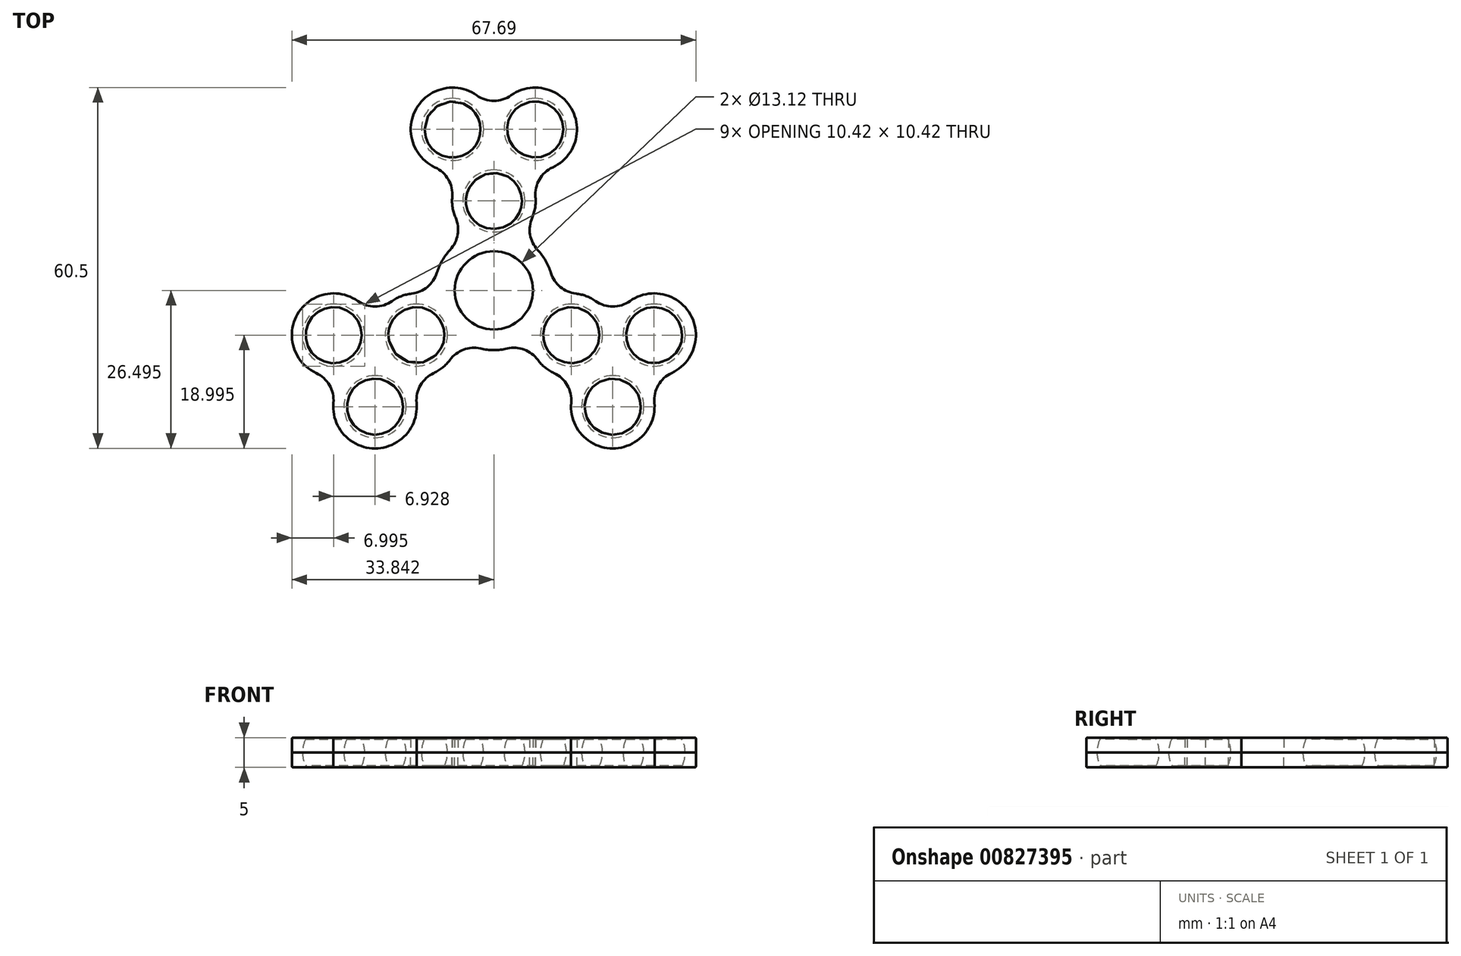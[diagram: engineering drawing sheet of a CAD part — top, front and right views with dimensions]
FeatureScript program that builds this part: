
annotation { "Feature Type Name" : "Feature", "Feature Type Description" : "" }
export const myFeature = defineFeature(function(context is Context, id is Id, definition is map)
    precondition{}
    {
        {
            var Q0;
            Q0=qCreatedBy(makeId("Top.planeOp"),FACE);
            var sketch = newSketch(context, id + "F0", { "sketchPlane" : qUnion([Q0])});
            skCircle(sketch, "E0", {"center": v(73.24, 0.6) * mm, "radius": 6.56 * mm});
            skArc(sketch, "E1", {"start": v(65.9, 7.4) * mm, "mid": v(64.58, 5.6) * mm, "end": v(63.69, 3.55) * mm});
            skCircle(sketch, "E2", {"center": v(73.24, 15.6) * mm, "radius": 2.5 * mm});
            skCircle(sketch, "E3", {"center": v(60.25, -6.9) * mm, "radius": 2.5 * mm});
            skCircle(sketch, "E4", {"center": v(86.23, -6.9) * mm, "radius": 2.5 * mm});
            skCircle(sketch, "E5", {"center": v(80.17, 27.6) * mm, "radius": 2.5 * mm});
            skCircle(sketch, "E6", {"center": v(66.31, 27.6) * mm, "radius": 2.5 * mm});
            skCircle(sketch, "E7", {"center": v(46.4, -6.9) * mm, "radius": 2.5 * mm});
            skCircle(sketch, "E8", {"center": v(53.32, -18.9) * mm, "radius": 2.5 * mm});
            skCircle(sketch, "E9", {"center": v(93.16, -18.9) * mm, "radius": 2.5 * mm});
            skCircle(sketch, "E10", {"center": v(100.09, -6.9) * mm, "radius": 2.5 * mm});
            skArc(sketch, "E11", {"start": v(66.27, 16.25) * mm, "mid": v(66.33, 14.5) * mm, "end": v(66.83, 12.8) * mm});
            skArc(sketch, "E12", {"start": v(70.36, 33.32) * mm, "mid": v(60.25, 31.1) * mm, "end": v(63.38, 21.25) * mm});
            skArc(sketch, "E13", {"start": v(83.1, 21.25) * mm, "mid": v(86.23, 31.1) * mm, "end": v(76.13, 33.32) * mm});
            skPoint(sketch, "E14.visualSharp", {"position": v(73.24, 28.6) * mm});
            skArc(sketch, "E14.filletArc", {"start": v(70.36, 33.32) * mm, "mid": v(73.24, 32.4) * mm, "end": v(76.13, 33.32) * mm});
            skPoint(sketch, "E15.visualSharp", {"position": v(68.91, 21.1) * mm});
            skArc(sketch, "E15.filletArc", {"start": v(66.27, 16.25) * mm, "mid": v(65.62, 19.2) * mm, "end": v(63.38, 21.25) * mm});
            skPoint(sketch, "E16.visualSharp", {"position": v(77.57, 21.1) * mm});
            skArc(sketch, "E16.filletArc", {"start": v(83.1, 21.25) * mm, "mid": v(80.86, 19.2) * mm, "end": v(80.21, 16.25) * mm});
            skArc(sketch, "E17.trimOffspring", {"start": v(79.66, 12.8) * mm, "mid": v(80.15, 14.5) * mm, "end": v(80.21, 16.25) * mm});
            skArc(sketch, "E18", {"start": v(63.18, -13.25) * mm, "mid": v(64.67, -12.32) * mm, "end": v(65.88, -11.05) * mm});
            skArc(sketch, "E19", {"start": v(46.35, -18.25) * mm, "mid": v(53.32, -25.9) * mm, "end": v(60.3, -18.25) * mm});
            skArc(sketch, "E20", {"start": v(50.44, -1.18) * mm, "mid": v(40.33, -3.4) * mm, "end": v(43.47, -13.25) * mm});
            skArc(sketch, "E21.filletArc", {"start": v(46.35, -18.25) * mm, "mid": v(45.7, -15.3) * mm, "end": v(43.47, -13.25) * mm});
            skArc(sketch, "E22.filletArc", {"start": v(63.18, -13.25) * mm, "mid": v(60.94, -15.3) * mm, "end": v(60.3, -18.25) * mm});
            skArc(sketch, "E23.filletArc", {"start": v(50.44, -1.18) * mm, "mid": v(53.32, -2.1) * mm, "end": v(56.21, -1.18) * mm});
            skArc(sketch, "E24.trimOffspring", {"start": v(59.47, 0.06) * mm, "mid": v(57.76, -0.35) * mm, "end": v(56.21, -1.18) * mm});
            skArc(sketch, "E25", {"start": v(90.27, -1.18) * mm, "mid": v(88.72, -0.35) * mm, "end": v(87.02, 0.06) * mm});
            skArc(sketch, "E26", {"start": v(103.02, -13.25) * mm, "mid": v(106.15, -3.4) * mm, "end": v(96.05, -1.18) * mm});
            skArc(sketch, "E27", {"start": v(86.2, -18.25) * mm, "mid": v(93.16, -25.9) * mm, "end": v(100.13, -18.25) * mm});
            skArc(sketch, "E28.filletArc", {"start": v(103.02, -13.25) * mm, "mid": v(100.78, -15.3) * mm, "end": v(100.13, -18.25) * mm});
            skArc(sketch, "E29.filletArc", {"start": v(90.27, -1.18) * mm, "mid": v(93.16, -2.1) * mm, "end": v(96.05, -1.18) * mm});
            skArc(sketch, "E30.filletArc", {"start": v(86.2, -18.25) * mm, "mid": v(85.54, -15.3) * mm, "end": v(83.3, -13.25) * mm});
            skArc(sketch, "E31.trimOffspring", {"start": v(80.6, -11.05) * mm, "mid": v(81.81, -12.32) * mm, "end": v(83.3, -13.25) * mm});
            skArc(sketch, "E32.trimOffspring", {"start": v(71.02, -9.14) * mm, "mid": v(73.24, -9.4) * mm, "end": v(75.46, -9.14) * mm});
            skArc(sketch, "E33.trimOffspring", {"start": v(82.8, 3.55) * mm, "mid": v(81.9, 5.6) * mm, "end": v(80.57, 7.4) * mm});
            skPoint(sketch, "E34.visualSharp", {"position": v(63.31, -0.6) * mm});
            skArc(sketch, "E34.filletArc", {"start": v(59.47, 0.06) * mm, "mid": v(62.1, 1.18) * mm, "end": v(63.69, 3.55) * mm});
            skPoint(sketch, "E35.visualSharp", {"position": v(67.23, -7.39) * mm});
            skArc(sketch, "E35.filletArc", {"start": v(71.02, -9.14) * mm, "mid": v(68.17, -9.33) * mm, "end": v(65.88, -11.05) * mm});
            skPoint(sketch, "E36.visualSharp", {"position": v(79.25, -7.39) * mm});
            skArc(sketch, "E36.filletArc", {"start": v(80.6, -11.05) * mm, "mid": v(78.32, -9.33) * mm, "end": v(75.46, -9.14) * mm});
            skPoint(sketch, "E37.visualSharp", {"position": v(83.17, -0.6) * mm});
            skArc(sketch, "E37.filletArc", {"start": v(82.8, 3.55) * mm, "mid": v(84.39, 1.18) * mm, "end": v(87.02, 0.06) * mm});
            skPoint(sketch, "E38.visualSharp", {"position": v(77.16, 9.8) * mm});
            skArc(sketch, "E38.filletArc", {"start": v(79.66, 12.8) * mm, "mid": v(79.31, 9.97) * mm, "end": v(80.57, 7.4) * mm});
            skPoint(sketch, "E39.visualSharp", {"position": v(69.32, 9.8) * mm});
            skArc(sketch, "E39.filletArc", {"start": v(65.9, 7.4) * mm, "mid": v(67.17, 9.97) * mm, "end": v(66.83, 12.8) * mm});
            skSolve(sketch);
        }
        {
            var Q0;
            Q0=qSketchRegion(id+"F0",true);
            extrude(context, id + "F1", {"entities" : qUnion([Q0]), "depth" : 2.5 * mm, "offsetDistance" : 25 * mm});
        }
        {
            var Q0;
            Q0=makeQuery(id+"F0.imprint","IMPRINT",FACE,{"disambiguationData":[TD([[makeQuery(id+"F0.imprint","IMPRINT",EDGE,{"derivedFrom":sQuery(id+"F0.wireOp",EDGE,"E0")}),-1.0]])]});
            extrude(context, id + "F2", {"entities" : qUnion([Q0]), "oppositeDirection" : true, "depth" : 2.5 * mm, "offsetDistance" : 25 * mm});
        }
        {
            var Q0;
            Q0=makeQuery(id+"F2.opExtrude","CAP_FACE",FACE,{"disambiguationData":[OSD([sQuery(id+"F0.wireOp",EDGE,"E0"),sQuery(id+"F0.wireOp",EDGE,"E1"),sQuery(id+"F0.wireOp",EDGE,"E2"),sQuery(id+"F0.wireOp",EDGE,"E3"),sQuery(id+"F0.wireOp",EDGE,"E4"),sQuery(id+"F0.wireOp",EDGE,"E5"),sQuery(id+"F0.wireOp",EDGE,"E6"),sQuery(id+"F0.wireOp",EDGE,"E7"),sQuery(id+"F0.wireOp",EDGE,"E8"),sQuery(id+"F0.wireOp",EDGE,"E9"),sQuery(id+"F0.wireOp",EDGE,"E10"),sQuery(id+"F0.wireOp",EDGE,"E11"),sQuery(id+"F0.wireOp",EDGE,"E12"),sQuery(id+"F0.wireOp",EDGE,"E13"),sQuery(id+"F0.wireOp",EDGE,"E14.filletArc"),sQuery(id+"F0.wireOp",EDGE,"E15.filletArc"),sQuery(id+"F0.wireOp",EDGE,"E16.filletArc"),sQuery(id+"F0.wireOp",EDGE,"E17.trimOffspring"),sQuery(id+"F0.wireOp",EDGE,"E18"),sQuery(id+"F0.wireOp",EDGE,"E19"),sQuery(id+"F0.wireOp",EDGE,"E20"),sQuery(id+"F0.wireOp",EDGE,"E21.filletArc"),sQuery(id+"F0.wireOp",EDGE,"E22.filletArc"),sQuery(id+"F0.wireOp",EDGE,"E23.filletArc"),sQuery(id+"F0.wireOp",EDGE,"E24.trimOffspring"),sQuery(id+"F0.wireOp",EDGE,"E25"),sQuery(id+"F0.wireOp",EDGE,"E26"),sQuery(id+"F0.wireOp",EDGE,"E27"),sQuery(id+"F0.wireOp",EDGE,"E28.filletArc"),sQuery(id+"F0.wireOp",EDGE,"E29.filletArc"),sQuery(id+"F0.wireOp",EDGE,"E30.filletArc"),sQuery(id+"F0.wireOp",EDGE,"E31.trimOffspring"),sQuery(id+"F0.wireOp",EDGE,"E32.trimOffspring"),sQuery(id+"F0.wireOp",EDGE,"E33.trimOffspring"),sQuery(id+"F0.wireOp",EDGE,"E34.filletArc"),sQuery(id+"F0.wireOp",EDGE,"E35.filletArc"),sQuery(id+"F0.wireOp",EDGE,"E36.filletArc"),sQuery(id+"F0.wireOp",EDGE,"E37.filletArc"),sQuery(id+"F0.wireOp",EDGE,"E38.filletArc"),sQuery(id+"F0.wireOp",EDGE,"E39.filletArc")])],"isStart":true});
            var sketch = newSketch(context, id + "F3", { "sketchPlane" : qUnion([Q0])});
            skLineSegment(sketch, "E40", {"start": v(53.32, -18.9) * mm, "end": v(53.32, -24.1) * mm});
            skLineSegment(sketch, "E41", {"start": v(53.32, -18.9) * mm, "end": v(53.32, -13.68) * mm});
            skArc(sketch, "E42", {"start": v(53.32, -13.68) * mm, "mid": v(48.11, -18.9) * mm, "end": v(53.32, -24.1) * mm});
            skSolve(sketch);
        }
        {
            var Q0;
            Q0=qSketchRegion(id+"F3",true);
            var Q1;
            Q1=sQuery(id+"F3.wireOp",EDGE,"E41");
            revolve(context, id + "F4", {"surfaceOperationType" : NewSurfaceOperationType.NEW, "entities" : qUnion([Q0]), "axis" : qUnion([Q1]), "revolveType" : RevolveType.FULL});
        }
        {
            var Q0;
            Q0=makeQuery(id+"F2.opExtrude","CAP_FACE",FACE,{"disambiguationData":[OSD([sQuery(id+"F0.wireOp",EDGE,"E0"),sQuery(id+"F0.wireOp",EDGE,"E1"),sQuery(id+"F0.wireOp",EDGE,"E2"),sQuery(id+"F0.wireOp",EDGE,"E3"),sQuery(id+"F0.wireOp",EDGE,"E4"),sQuery(id+"F0.wireOp",EDGE,"E5"),sQuery(id+"F0.wireOp",EDGE,"E6"),sQuery(id+"F0.wireOp",EDGE,"E7"),sQuery(id+"F0.wireOp",EDGE,"E8"),sQuery(id+"F0.wireOp",EDGE,"E9"),sQuery(id+"F0.wireOp",EDGE,"E10"),sQuery(id+"F0.wireOp",EDGE,"E11"),sQuery(id+"F0.wireOp",EDGE,"E12"),sQuery(id+"F0.wireOp",EDGE,"E13"),sQuery(id+"F0.wireOp",EDGE,"E14.filletArc"),sQuery(id+"F0.wireOp",EDGE,"E15.filletArc"),sQuery(id+"F0.wireOp",EDGE,"E16.filletArc"),sQuery(id+"F0.wireOp",EDGE,"E17.trimOffspring"),sQuery(id+"F0.wireOp",EDGE,"E18"),sQuery(id+"F0.wireOp",EDGE,"E19"),sQuery(id+"F0.wireOp",EDGE,"E20"),sQuery(id+"F0.wireOp",EDGE,"E21.filletArc"),sQuery(id+"F0.wireOp",EDGE,"E22.filletArc"),sQuery(id+"F0.wireOp",EDGE,"E23.filletArc"),sQuery(id+"F0.wireOp",EDGE,"E24.trimOffspring"),sQuery(id+"F0.wireOp",EDGE,"E25"),sQuery(id+"F0.wireOp",EDGE,"E26"),sQuery(id+"F0.wireOp",EDGE,"E27"),sQuery(id+"F0.wireOp",EDGE,"E28.filletArc"),sQuery(id+"F0.wireOp",EDGE,"E29.filletArc"),sQuery(id+"F0.wireOp",EDGE,"E30.filletArc"),sQuery(id+"F0.wireOp",EDGE,"E31.trimOffspring"),sQuery(id+"F0.wireOp",EDGE,"E32.trimOffspring"),sQuery(id+"F0.wireOp",EDGE,"E33.trimOffspring"),sQuery(id+"F0.wireOp",EDGE,"E34.filletArc"),sQuery(id+"F0.wireOp",EDGE,"E35.filletArc"),sQuery(id+"F0.wireOp",EDGE,"E36.filletArc"),sQuery(id+"F0.wireOp",EDGE,"E37.filletArc"),sQuery(id+"F0.wireOp",EDGE,"E38.filletArc"),sQuery(id+"F0.wireOp",EDGE,"E39.filletArc")])],"isStart":true});
            var sketch = newSketch(context, id + "F5", { "sketchPlane" : qUnion([Q0])});
            skLineSegment(sketch, "E43", {"start": v(60.25, -6.9) * mm, "end": v(60.25, -12.1) * mm});
            skLineSegment(sketch, "E44", {"start": v(60.25, -6.9) * mm, "end": v(60.25, -1.68) * mm});
            skArc(sketch, "E45", {"start": v(60.25, -1.68) * mm, "mid": v(55.04, -6.9) * mm, "end": v(60.25, -12.1) * mm});
            skSolve(sketch);
        }
        {
            var Q0;
            Q0=makeQuery(id+"F2.opExtrude","CAP_FACE",FACE,{"disambiguationData":[OSD([sQuery(id+"F0.wireOp",EDGE,"E0"),sQuery(id+"F0.wireOp",EDGE,"E1"),sQuery(id+"F0.wireOp",EDGE,"E2"),sQuery(id+"F0.wireOp",EDGE,"E3"),sQuery(id+"F0.wireOp",EDGE,"E4"),sQuery(id+"F0.wireOp",EDGE,"E5"),sQuery(id+"F0.wireOp",EDGE,"E6"),sQuery(id+"F0.wireOp",EDGE,"E7"),sQuery(id+"F0.wireOp",EDGE,"E8"),sQuery(id+"F0.wireOp",EDGE,"E9"),sQuery(id+"F0.wireOp",EDGE,"E10"),sQuery(id+"F0.wireOp",EDGE,"E11"),sQuery(id+"F0.wireOp",EDGE,"E12"),sQuery(id+"F0.wireOp",EDGE,"E13"),sQuery(id+"F0.wireOp",EDGE,"E14.filletArc"),sQuery(id+"F0.wireOp",EDGE,"E15.filletArc"),sQuery(id+"F0.wireOp",EDGE,"E16.filletArc"),sQuery(id+"F0.wireOp",EDGE,"E17.trimOffspring"),sQuery(id+"F0.wireOp",EDGE,"E18"),sQuery(id+"F0.wireOp",EDGE,"E19"),sQuery(id+"F0.wireOp",EDGE,"E20"),sQuery(id+"F0.wireOp",EDGE,"E21.filletArc"),sQuery(id+"F0.wireOp",EDGE,"E22.filletArc"),sQuery(id+"F0.wireOp",EDGE,"E23.filletArc"),sQuery(id+"F0.wireOp",EDGE,"E24.trimOffspring"),sQuery(id+"F0.wireOp",EDGE,"E25"),sQuery(id+"F0.wireOp",EDGE,"E26"),sQuery(id+"F0.wireOp",EDGE,"E27"),sQuery(id+"F0.wireOp",EDGE,"E28.filletArc"),sQuery(id+"F0.wireOp",EDGE,"E29.filletArc"),sQuery(id+"F0.wireOp",EDGE,"E30.filletArc"),sQuery(id+"F0.wireOp",EDGE,"E31.trimOffspring"),sQuery(id+"F0.wireOp",EDGE,"E32.trimOffspring"),sQuery(id+"F0.wireOp",EDGE,"E33.trimOffspring"),sQuery(id+"F0.wireOp",EDGE,"E34.filletArc"),sQuery(id+"F0.wireOp",EDGE,"E35.filletArc"),sQuery(id+"F0.wireOp",EDGE,"E36.filletArc"),sQuery(id+"F0.wireOp",EDGE,"E37.filletArc"),sQuery(id+"F0.wireOp",EDGE,"E38.filletArc"),sQuery(id+"F0.wireOp",EDGE,"E39.filletArc")])],"isStart":true});
            var sketch = newSketch(context, id + "F6", { "sketchPlane" : qUnion([Q0])});
            skLineSegment(sketch, "E46", {"start": v(93.16, -18.9) * mm, "end": v(93.16, -24.1) * mm});
            skArc(sketch, "E47", {"start": v(93.16, -13.68) * mm, "mid": v(87.95, -18.9) * mm, "end": v(93.16, -24.1) * mm});
            skLineSegment(sketch, "E48", {"start": v(93.16, -18.9) * mm, "end": v(93.16, -13.68) * mm});
            skSolve(sketch);
        }
        {
            var Q0;
            Q0=qSketchRegion(id+"F6",true);
            var Q1;
            Q1=sQuery(id+"F6.wireOp",EDGE,"E48");
            revolve(context, id + "F7", {"surfaceOperationType" : NewSurfaceOperationType.NEW, "entities" : qUnion([Q0]), "axis" : qUnion([Q1]), "revolveType" : RevolveType.FULL});
        }
        {
            var Q0;
            Q0=makeQuery(id+"F2.opExtrude","CAP_FACE",FACE,{"disambiguationData":[OSD([sQuery(id+"F0.wireOp",EDGE,"E0"),sQuery(id+"F0.wireOp",EDGE,"E1"),sQuery(id+"F0.wireOp",EDGE,"E2"),sQuery(id+"F0.wireOp",EDGE,"E3"),sQuery(id+"F0.wireOp",EDGE,"E4"),sQuery(id+"F0.wireOp",EDGE,"E5"),sQuery(id+"F0.wireOp",EDGE,"E6"),sQuery(id+"F0.wireOp",EDGE,"E7"),sQuery(id+"F0.wireOp",EDGE,"E8"),sQuery(id+"F0.wireOp",EDGE,"E9"),sQuery(id+"F0.wireOp",EDGE,"E10"),sQuery(id+"F0.wireOp",EDGE,"E11"),sQuery(id+"F0.wireOp",EDGE,"E12"),sQuery(id+"F0.wireOp",EDGE,"E13"),sQuery(id+"F0.wireOp",EDGE,"E14.filletArc"),sQuery(id+"F0.wireOp",EDGE,"E15.filletArc"),sQuery(id+"F0.wireOp",EDGE,"E16.filletArc"),sQuery(id+"F0.wireOp",EDGE,"E17.trimOffspring"),sQuery(id+"F0.wireOp",EDGE,"E18"),sQuery(id+"F0.wireOp",EDGE,"E19"),sQuery(id+"F0.wireOp",EDGE,"E20"),sQuery(id+"F0.wireOp",EDGE,"E21.filletArc"),sQuery(id+"F0.wireOp",EDGE,"E22.filletArc"),sQuery(id+"F0.wireOp",EDGE,"E23.filletArc"),sQuery(id+"F0.wireOp",EDGE,"E24.trimOffspring"),sQuery(id+"F0.wireOp",EDGE,"E25"),sQuery(id+"F0.wireOp",EDGE,"E26"),sQuery(id+"F0.wireOp",EDGE,"E27"),sQuery(id+"F0.wireOp",EDGE,"E28.filletArc"),sQuery(id+"F0.wireOp",EDGE,"E29.filletArc"),sQuery(id+"F0.wireOp",EDGE,"E30.filletArc"),sQuery(id+"F0.wireOp",EDGE,"E31.trimOffspring"),sQuery(id+"F0.wireOp",EDGE,"E32.trimOffspring"),sQuery(id+"F0.wireOp",EDGE,"E33.trimOffspring"),sQuery(id+"F0.wireOp",EDGE,"E34.filletArc"),sQuery(id+"F0.wireOp",EDGE,"E35.filletArc"),sQuery(id+"F0.wireOp",EDGE,"E36.filletArc"),sQuery(id+"F0.wireOp",EDGE,"E37.filletArc"),sQuery(id+"F0.wireOp",EDGE,"E38.filletArc"),sQuery(id+"F0.wireOp",EDGE,"E39.filletArc")])],"isStart":true});
            var sketch = newSketch(context, id + "F8", { "sketchPlane" : qUnion([Q0])});
            skLineSegment(sketch, "E49", {"start": v(86.23, -6.9) * mm, "end": v(86.23, -12.1) * mm});
            skArc(sketch, "E50", {"start": v(86.23, -1.68) * mm, "mid": v(81.02, -6.9) * mm, "end": v(86.23, -12.1) * mm});
            skLineSegment(sketch, "E51", {"start": v(86.23, -6.9) * mm, "end": v(86.23, -1.68) * mm});
            skSolve(sketch);
        }
        {
            var Q0;
            Q0=qSketchRegion(id+"F8",true);
            var Q1;
            Q1=sQuery(id+"F8.wireOp",EDGE,"E51");
            revolve(context, id + "F9", {"surfaceOperationType" : NewSurfaceOperationType.NEW, "entities" : qUnion([Q0]), "axis" : qUnion([Q1]), "revolveType" : RevolveType.FULL});
        }
        {
            var Q0;
            Q0=makeQuery(id+"F2.opExtrude","CAP_FACE",FACE,{"disambiguationData":[OSD([sQuery(id+"F0.wireOp",EDGE,"E0"),sQuery(id+"F0.wireOp",EDGE,"E1"),sQuery(id+"F0.wireOp",EDGE,"E2"),sQuery(id+"F0.wireOp",EDGE,"E3"),sQuery(id+"F0.wireOp",EDGE,"E4"),sQuery(id+"F0.wireOp",EDGE,"E5"),sQuery(id+"F0.wireOp",EDGE,"E6"),sQuery(id+"F0.wireOp",EDGE,"E7"),sQuery(id+"F0.wireOp",EDGE,"E8"),sQuery(id+"F0.wireOp",EDGE,"E9"),sQuery(id+"F0.wireOp",EDGE,"E10"),sQuery(id+"F0.wireOp",EDGE,"E11"),sQuery(id+"F0.wireOp",EDGE,"E12"),sQuery(id+"F0.wireOp",EDGE,"E13"),sQuery(id+"F0.wireOp",EDGE,"E14.filletArc"),sQuery(id+"F0.wireOp",EDGE,"E15.filletArc"),sQuery(id+"F0.wireOp",EDGE,"E16.filletArc"),sQuery(id+"F0.wireOp",EDGE,"E17.trimOffspring"),sQuery(id+"F0.wireOp",EDGE,"E18"),sQuery(id+"F0.wireOp",EDGE,"E19"),sQuery(id+"F0.wireOp",EDGE,"E20"),sQuery(id+"F0.wireOp",EDGE,"E21.filletArc"),sQuery(id+"F0.wireOp",EDGE,"E22.filletArc"),sQuery(id+"F0.wireOp",EDGE,"E23.filletArc"),sQuery(id+"F0.wireOp",EDGE,"E24.trimOffspring"),sQuery(id+"F0.wireOp",EDGE,"E25"),sQuery(id+"F0.wireOp",EDGE,"E26"),sQuery(id+"F0.wireOp",EDGE,"E27"),sQuery(id+"F0.wireOp",EDGE,"E28.filletArc"),sQuery(id+"F0.wireOp",EDGE,"E29.filletArc"),sQuery(id+"F0.wireOp",EDGE,"E30.filletArc"),sQuery(id+"F0.wireOp",EDGE,"E31.trimOffspring"),sQuery(id+"F0.wireOp",EDGE,"E32.trimOffspring"),sQuery(id+"F0.wireOp",EDGE,"E33.trimOffspring"),sQuery(id+"F0.wireOp",EDGE,"E34.filletArc"),sQuery(id+"F0.wireOp",EDGE,"E35.filletArc"),sQuery(id+"F0.wireOp",EDGE,"E36.filletArc"),sQuery(id+"F0.wireOp",EDGE,"E37.filletArc"),sQuery(id+"F0.wireOp",EDGE,"E38.filletArc"),sQuery(id+"F0.wireOp",EDGE,"E39.filletArc")])],"isStart":true});
            var sketch = newSketch(context, id + "F10", { "sketchPlane" : qUnion([Q0])});
            skLineSegment(sketch, "E52", {"start": v(100.09, -6.9) * mm, "end": v(100.09, -12.1) * mm});
            skArc(sketch, "E53", {"start": v(100.09, -1.68) * mm, "mid": v(94.88, -6.9) * mm, "end": v(100.09, -12.1) * mm});
            skLineSegment(sketch, "E54", {"start": v(100.09, -6.9) * mm, "end": v(100.09, -1.68) * mm});
            skSolve(sketch);
        }
        {
            var Q0;
            Q0=qSketchRegion(id+"F10",true);
            var Q1;
            Q1=sQuery(id+"F10.wireOp",EDGE,"E52");
            revolve(context, id + "F11", {"surfaceOperationType" : NewSurfaceOperationType.NEW, "entities" : qUnion([Q0]), "axis" : qUnion([Q1]), "revolveType" : RevolveType.FULL});
        }
        {
            var Q0;
            Q0=makeQuery(id+"F2.opExtrude","CAP_FACE",FACE,{"disambiguationData":[OSD([sQuery(id+"F0.wireOp",EDGE,"E0"),sQuery(id+"F0.wireOp",EDGE,"E1"),sQuery(id+"F0.wireOp",EDGE,"E2"),sQuery(id+"F0.wireOp",EDGE,"E3"),sQuery(id+"F0.wireOp",EDGE,"E4"),sQuery(id+"F0.wireOp",EDGE,"E5"),sQuery(id+"F0.wireOp",EDGE,"E6"),sQuery(id+"F0.wireOp",EDGE,"E7"),sQuery(id+"F0.wireOp",EDGE,"E8"),sQuery(id+"F0.wireOp",EDGE,"E9"),sQuery(id+"F0.wireOp",EDGE,"E10"),sQuery(id+"F0.wireOp",EDGE,"E11"),sQuery(id+"F0.wireOp",EDGE,"E12"),sQuery(id+"F0.wireOp",EDGE,"E13"),sQuery(id+"F0.wireOp",EDGE,"E14.filletArc"),sQuery(id+"F0.wireOp",EDGE,"E15.filletArc"),sQuery(id+"F0.wireOp",EDGE,"E16.filletArc"),sQuery(id+"F0.wireOp",EDGE,"E17.trimOffspring"),sQuery(id+"F0.wireOp",EDGE,"E18"),sQuery(id+"F0.wireOp",EDGE,"E19"),sQuery(id+"F0.wireOp",EDGE,"E20"),sQuery(id+"F0.wireOp",EDGE,"E21.filletArc"),sQuery(id+"F0.wireOp",EDGE,"E22.filletArc"),sQuery(id+"F0.wireOp",EDGE,"E23.filletArc"),sQuery(id+"F0.wireOp",EDGE,"E24.trimOffspring"),sQuery(id+"F0.wireOp",EDGE,"E25"),sQuery(id+"F0.wireOp",EDGE,"E26"),sQuery(id+"F0.wireOp",EDGE,"E27"),sQuery(id+"F0.wireOp",EDGE,"E28.filletArc"),sQuery(id+"F0.wireOp",EDGE,"E29.filletArc"),sQuery(id+"F0.wireOp",EDGE,"E30.filletArc"),sQuery(id+"F0.wireOp",EDGE,"E31.trimOffspring"),sQuery(id+"F0.wireOp",EDGE,"E32.trimOffspring"),sQuery(id+"F0.wireOp",EDGE,"E33.trimOffspring"),sQuery(id+"F0.wireOp",EDGE,"E34.filletArc"),sQuery(id+"F0.wireOp",EDGE,"E35.filletArc"),sQuery(id+"F0.wireOp",EDGE,"E36.filletArc"),sQuery(id+"F0.wireOp",EDGE,"E37.filletArc"),sQuery(id+"F0.wireOp",EDGE,"E38.filletArc"),sQuery(id+"F0.wireOp",EDGE,"E39.filletArc")])],"isStart":true});
            var sketch = newSketch(context, id + "F12", { "sketchPlane" : qUnion([Q0])});
            skLineSegment(sketch, "E55", {"start": v(73.24, 15.6) * mm, "end": v(73.24, 10.4) * mm});
            skArc(sketch, "E56", {"start": v(73.24, 20.82) * mm, "mid": v(68.03, 15.6) * mm, "end": v(73.24, 10.4) * mm});
            skLineSegment(sketch, "E57", {"start": v(73.24, 15.6) * mm, "end": v(73.24, 20.82) * mm});
            skSolve(sketch);
        }
        {
            var Q0;
            Q0=qSketchRegion(id+"F12",true);
            var Q1;
            Q1=sQuery(id+"F12.wireOp",EDGE,"E55");
            revolve(context, id + "F13", {"surfaceOperationType" : NewSurfaceOperationType.NEW, "entities" : qUnion([Q0]), "axis" : qUnion([Q1]), "revolveType" : RevolveType.FULL});
        }
        {
            var Q0;
            Q0=makeQuery(id+"F2.opExtrude","CAP_FACE",FACE,{"disambiguationData":[OSD([sQuery(id+"F0.wireOp",EDGE,"E0"),sQuery(id+"F0.wireOp",EDGE,"E1"),sQuery(id+"F0.wireOp",EDGE,"E2"),sQuery(id+"F0.wireOp",EDGE,"E3"),sQuery(id+"F0.wireOp",EDGE,"E4"),sQuery(id+"F0.wireOp",EDGE,"E5"),sQuery(id+"F0.wireOp",EDGE,"E6"),sQuery(id+"F0.wireOp",EDGE,"E7"),sQuery(id+"F0.wireOp",EDGE,"E8"),sQuery(id+"F0.wireOp",EDGE,"E9"),sQuery(id+"F0.wireOp",EDGE,"E10"),sQuery(id+"F0.wireOp",EDGE,"E11"),sQuery(id+"F0.wireOp",EDGE,"E12"),sQuery(id+"F0.wireOp",EDGE,"E13"),sQuery(id+"F0.wireOp",EDGE,"E14.filletArc"),sQuery(id+"F0.wireOp",EDGE,"E15.filletArc"),sQuery(id+"F0.wireOp",EDGE,"E16.filletArc"),sQuery(id+"F0.wireOp",EDGE,"E17.trimOffspring"),sQuery(id+"F0.wireOp",EDGE,"E18"),sQuery(id+"F0.wireOp",EDGE,"E19"),sQuery(id+"F0.wireOp",EDGE,"E20"),sQuery(id+"F0.wireOp",EDGE,"E21.filletArc"),sQuery(id+"F0.wireOp",EDGE,"E22.filletArc"),sQuery(id+"F0.wireOp",EDGE,"E23.filletArc"),sQuery(id+"F0.wireOp",EDGE,"E24.trimOffspring"),sQuery(id+"F0.wireOp",EDGE,"E25"),sQuery(id+"F0.wireOp",EDGE,"E26"),sQuery(id+"F0.wireOp",EDGE,"E27"),sQuery(id+"F0.wireOp",EDGE,"E28.filletArc"),sQuery(id+"F0.wireOp",EDGE,"E29.filletArc"),sQuery(id+"F0.wireOp",EDGE,"E30.filletArc"),sQuery(id+"F0.wireOp",EDGE,"E31.trimOffspring"),sQuery(id+"F0.wireOp",EDGE,"E32.trimOffspring"),sQuery(id+"F0.wireOp",EDGE,"E33.trimOffspring"),sQuery(id+"F0.wireOp",EDGE,"E34.filletArc"),sQuery(id+"F0.wireOp",EDGE,"E35.filletArc"),sQuery(id+"F0.wireOp",EDGE,"E36.filletArc"),sQuery(id+"F0.wireOp",EDGE,"E37.filletArc"),sQuery(id+"F0.wireOp",EDGE,"E38.filletArc"),sQuery(id+"F0.wireOp",EDGE,"E39.filletArc")])],"isStart":true});
            var sketch = newSketch(context, id + "F14", { "sketchPlane" : qUnion([Q0])});
            skLineSegment(sketch, "E58", {"start": v(66.31, 27.6) * mm, "end": v(66.31, 22.4) * mm});
            skArc(sketch, "E59", {"start": v(66.31, 32.82) * mm, "mid": v(61.1, 27.6) * mm, "end": v(66.31, 22.4) * mm});
            skLineSegment(sketch, "E60", {"start": v(66.31, 27.6) * mm, "end": v(66.31, 32.82) * mm});
            skSolve(sketch);
        }
        {
            var Q0;
            Q0=qSketchRegion(id+"F14",true);
            var Q1;
            Q1=sQuery(id+"F14.wireOp",EDGE,"E58");
            revolve(context, id + "F15", {"surfaceOperationType" : NewSurfaceOperationType.NEW, "entities" : qUnion([Q0]), "axis" : qUnion([Q1]), "revolveType" : RevolveType.FULL});
        }
        {
            var Q0;
            Q0=makeQuery(id+"F2.opExtrude","CAP_FACE",FACE,{"disambiguationData":[OSD([sQuery(id+"F0.wireOp",EDGE,"E0"),sQuery(id+"F0.wireOp",EDGE,"E1"),sQuery(id+"F0.wireOp",EDGE,"E2"),sQuery(id+"F0.wireOp",EDGE,"E3"),sQuery(id+"F0.wireOp",EDGE,"E4"),sQuery(id+"F0.wireOp",EDGE,"E5"),sQuery(id+"F0.wireOp",EDGE,"E6"),sQuery(id+"F0.wireOp",EDGE,"E7"),sQuery(id+"F0.wireOp",EDGE,"E8"),sQuery(id+"F0.wireOp",EDGE,"E9"),sQuery(id+"F0.wireOp",EDGE,"E10"),sQuery(id+"F0.wireOp",EDGE,"E11"),sQuery(id+"F0.wireOp",EDGE,"E12"),sQuery(id+"F0.wireOp",EDGE,"E13"),sQuery(id+"F0.wireOp",EDGE,"E14.filletArc"),sQuery(id+"F0.wireOp",EDGE,"E15.filletArc"),sQuery(id+"F0.wireOp",EDGE,"E16.filletArc"),sQuery(id+"F0.wireOp",EDGE,"E17.trimOffspring"),sQuery(id+"F0.wireOp",EDGE,"E18"),sQuery(id+"F0.wireOp",EDGE,"E19"),sQuery(id+"F0.wireOp",EDGE,"E20"),sQuery(id+"F0.wireOp",EDGE,"E21.filletArc"),sQuery(id+"F0.wireOp",EDGE,"E22.filletArc"),sQuery(id+"F0.wireOp",EDGE,"E23.filletArc"),sQuery(id+"F0.wireOp",EDGE,"E24.trimOffspring"),sQuery(id+"F0.wireOp",EDGE,"E25"),sQuery(id+"F0.wireOp",EDGE,"E26"),sQuery(id+"F0.wireOp",EDGE,"E27"),sQuery(id+"F0.wireOp",EDGE,"E28.filletArc"),sQuery(id+"F0.wireOp",EDGE,"E29.filletArc"),sQuery(id+"F0.wireOp",EDGE,"E30.filletArc"),sQuery(id+"F0.wireOp",EDGE,"E31.trimOffspring"),sQuery(id+"F0.wireOp",EDGE,"E32.trimOffspring"),sQuery(id+"F0.wireOp",EDGE,"E33.trimOffspring"),sQuery(id+"F0.wireOp",EDGE,"E34.filletArc"),sQuery(id+"F0.wireOp",EDGE,"E35.filletArc"),sQuery(id+"F0.wireOp",EDGE,"E36.filletArc"),sQuery(id+"F0.wireOp",EDGE,"E37.filletArc"),sQuery(id+"F0.wireOp",EDGE,"E38.filletArc"),sQuery(id+"F0.wireOp",EDGE,"E39.filletArc")])],"isStart":true});
            var sketch = newSketch(context, id + "F16", { "sketchPlane" : qUnion([Q0])});
            skLineSegment(sketch, "E61", {"start": v(80.17, 27.6) * mm, "end": v(80.17, 22.4) * mm});
            skArc(sketch, "E62", {"start": v(80.17, 32.82) * mm, "mid": v(74.96, 27.6) * mm, "end": v(80.17, 22.4) * mm});
            skLineSegment(sketch, "E63", {"start": v(80.17, 27.6) * mm, "end": v(80.17, 32.82) * mm});
            skSolve(sketch);
        }
        {
            var Q0;
            {var subQ0=sQuery(id+"F5.wireOp",EDGE,"E45");Q0=makeQuery(id+"F5.imprint","IMPRINT",FACE,{"disambiguationData":[TD([[makeQuery(id+"F5.imprint","IMPRINT",EDGE,{"derivedFrom":subQ0}),1.0]])]});}
            var Q1;
            {var subQ0=sQuery(id+"F5.wireOp",EDGE,"E44");var subQ1=sQuery(id+"F5.wireOp",EDGE,"E43");var subQ2=makeQuery(id+"F5.imprint","INTERSECT",VERTEX,{"derivedFrom":[subQ1,subQ0]});Q1=makeQuery(id+"F5.imprint","IMPRINT",FACE,{"disambiguationData":[TD([[makeQuery(id+"F5.imprint","IMPRINT",EDGE,{"disambiguationData":[TD([[subQ2,-1.0]])],"derivedFrom":subQ1}),-1.0]])]});}
            var Q2;
            Q2=sQuery(id+"F5.wireOp",EDGE,"E44");
            revolve(context, id + "F17", {"surfaceOperationType" : NewSurfaceOperationType.NEW, "entities" : qUnion([Q0, Q1]), "axis" : qUnion([Q2]), "revolveType" : RevolveType.FULL});
        }
        {
            var Q0;
            {var subQ0=sQuery(id+"F16.wireOp",EDGE,"E62");Q0=makeQuery(id+"F16.imprint","IMPRINT",FACE,{"disambiguationData":[TD([[makeQuery(id+"F16.imprint","IMPRINT",EDGE,{"derivedFrom":subQ0}),1.0]])]});}
            var Q1;
            {var subQ0=sQuery(id+"F16.wireOp",EDGE,"E63");var subQ1=sQuery(id+"F16.wireOp",EDGE,"E61");var subQ2=makeQuery(id+"F16.imprint","INTERSECT",VERTEX,{"derivedFrom":[subQ1,subQ0]});Q1=makeQuery(id+"F16.imprint","IMPRINT",FACE,{"disambiguationData":[TD([[makeQuery(id+"F16.imprint","IMPRINT",EDGE,{"disambiguationData":[TD([[subQ2,-1.0]])],"derivedFrom":subQ1}),-1.0]])]});}
            var Q2;
            Q2=sQuery(id+"F16.wireOp",EDGE,"E61");
            revolve(context, id + "F18", {"surfaceOperationType" : NewSurfaceOperationType.NEW, "entities" : qUnion([Q0, Q1]), "axis" : qUnion([Q2]), "revolveType" : RevolveType.FULL});
        }
        {
            var Q0;
            Q0=makeQuery(id+"F2.opExtrude","CAP_FACE",FACE,{"disambiguationData":[OSD([sQuery(id+"F0.wireOp",EDGE,"E0"),sQuery(id+"F0.wireOp",EDGE,"E1"),sQuery(id+"F0.wireOp",EDGE,"E2"),sQuery(id+"F0.wireOp",EDGE,"E3"),sQuery(id+"F0.wireOp",EDGE,"E4"),sQuery(id+"F0.wireOp",EDGE,"E5"),sQuery(id+"F0.wireOp",EDGE,"E6"),sQuery(id+"F0.wireOp",EDGE,"E7"),sQuery(id+"F0.wireOp",EDGE,"E8"),sQuery(id+"F0.wireOp",EDGE,"E9"),sQuery(id+"F0.wireOp",EDGE,"E10"),sQuery(id+"F0.wireOp",EDGE,"E11"),sQuery(id+"F0.wireOp",EDGE,"E12"),sQuery(id+"F0.wireOp",EDGE,"E13"),sQuery(id+"F0.wireOp",EDGE,"E14.filletArc"),sQuery(id+"F0.wireOp",EDGE,"E15.filletArc"),sQuery(id+"F0.wireOp",EDGE,"E16.filletArc"),sQuery(id+"F0.wireOp",EDGE,"E17.trimOffspring"),sQuery(id+"F0.wireOp",EDGE,"E18"),sQuery(id+"F0.wireOp",EDGE,"E19"),sQuery(id+"F0.wireOp",EDGE,"E20"),sQuery(id+"F0.wireOp",EDGE,"E21.filletArc"),sQuery(id+"F0.wireOp",EDGE,"E22.filletArc"),sQuery(id+"F0.wireOp",EDGE,"E23.filletArc"),sQuery(id+"F0.wireOp",EDGE,"E24.trimOffspring"),sQuery(id+"F0.wireOp",EDGE,"E25"),sQuery(id+"F0.wireOp",EDGE,"E26"),sQuery(id+"F0.wireOp",EDGE,"E27"),sQuery(id+"F0.wireOp",EDGE,"E28.filletArc"),sQuery(id+"F0.wireOp",EDGE,"E29.filletArc"),sQuery(id+"F0.wireOp",EDGE,"E30.filletArc"),sQuery(id+"F0.wireOp",EDGE,"E31.trimOffspring"),sQuery(id+"F0.wireOp",EDGE,"E32.trimOffspring"),sQuery(id+"F0.wireOp",EDGE,"E33.trimOffspring"),sQuery(id+"F0.wireOp",EDGE,"E34.filletArc"),sQuery(id+"F0.wireOp",EDGE,"E35.filletArc"),sQuery(id+"F0.wireOp",EDGE,"E36.filletArc"),sQuery(id+"F0.wireOp",EDGE,"E37.filletArc"),sQuery(id+"F0.wireOp",EDGE,"E38.filletArc"),sQuery(id+"F0.wireOp",EDGE,"E39.filletArc")])],"isStart":true});
            var sketch = newSketch(context, id + "F19", { "sketchPlane" : qUnion([Q0])});
            skLineSegment(sketch, "E64", {"start": v(46.4, -6.9) * mm, "end": v(46.4, -12.1) * mm});
            skArc(sketch, "E65", {"start": v(46.4, -1.68) * mm, "mid": v(41.19, -6.9) * mm, "end": v(46.4, -12.1) * mm});
            skLineSegment(sketch, "E66", {"start": v(46.4, -6.9) * mm, "end": v(46.4, -1.68) * mm});
            skSolve(sketch);
        }
        {
            var Q0;
            Q0=qSketchRegion(id+"F19",true);
            var Q1;
            Q1=sQuery(id+"F19.wireOp",EDGE,"E64");
            revolve(context, id + "F20", {"surfaceOperationType" : NewSurfaceOperationType.NEW, "entities" : qUnion([Q0]), "axis" : qUnion([Q1]), "revolveType" : RevolveType.FULL});
        }
        {
            var Q0;
            Q0=makeQuery(id+"F15.opRevolve","SWEPT_BODY",BODY,{"disambiguationData":[OSD([sQuery(id+"F14.wireOp",EDGE,"E58"),sQuery(id+"F14.wireOp",EDGE,"E59"),sQuery(id+"F14.wireOp",EDGE,"E60")])]});
            var Q1;
            Q1=makeQuery(id+"F18.opRevolve","SWEPT_BODY",BODY,{"disambiguationData":[OSD([sQuery(id+"F16.wireOp",EDGE,"E61"),sQuery(id+"F16.wireOp",EDGE,"E62"),sQuery(id+"F16.wireOp",EDGE,"E63")])]});
            var Q2;
            Q2=makeQuery(id+"F13.opRevolve","SWEPT_BODY",BODY,{"disambiguationData":[OSD([sQuery(id+"F12.wireOp",EDGE,"E55"),sQuery(id+"F12.wireOp",EDGE,"E56"),sQuery(id+"F12.wireOp",EDGE,"E57")])]});
            var Q3;
            Q3=makeQuery(id+"F9.opRevolve","SWEPT_BODY",BODY,{"disambiguationData":[OSD([sQuery(id+"F8.wireOp",EDGE,"E49"),sQuery(id+"F8.wireOp",EDGE,"E50"),sQuery(id+"F8.wireOp",EDGE,"E51")])]});
            var Q4;
            Q4=makeQuery(id+"F11.opRevolve","SWEPT_BODY",BODY,{"disambiguationData":[OSD([sQuery(id+"F10.wireOp",EDGE,"E52"),sQuery(id+"F10.wireOp",EDGE,"E53"),sQuery(id+"F10.wireOp",EDGE,"E54")])]});
            var Q5;
            Q5=makeQuery(id+"F20.opRevolve","SWEPT_BODY",BODY,{"disambiguationData":[OSD([sQuery(id+"F19.wireOp",EDGE,"E64"),sQuery(id+"F19.wireOp",EDGE,"E65"),sQuery(id+"F19.wireOp",EDGE,"E66")])]});
            var Q6;
            Q6=makeQuery(id+"F17.opRevolve","SWEPT_BODY",BODY,{"disambiguationData":[OSD([sQuery(id+"F5.wireOp",EDGE,"E43"),sQuery(id+"F5.wireOp",EDGE,"E44"),sQuery(id+"F5.wireOp",EDGE,"E45")])]});
            var Q7;
            Q7=makeQuery(id+"F4.opRevolve","SWEPT_BODY",BODY,{"disambiguationData":[OSD([sQuery(id+"F3.wireOp",EDGE,"E40"),sQuery(id+"F3.wireOp",EDGE,"E41"),sQuery(id+"F3.wireOp",EDGE,"E42")])]});
            var Q8;
            Q8=makeQuery(id+"F7.opRevolve","SWEPT_BODY",BODY,{"disambiguationData":[OSD([sQuery(id+"F6.wireOp",EDGE,"E46"),sQuery(id+"F6.wireOp",EDGE,"E47"),sQuery(id+"F6.wireOp",EDGE,"E48")])]});
            var Q9;
            Q9=makeQuery(id+"F1.opExtrude","SWEPT_BODY",BODY,{"disambiguationData":[OSD([sQuery(id+"F0.wireOp",EDGE,"E0"),sQuery(id+"F0.wireOp",EDGE,"E1"),sQuery(id+"F0.wireOp",EDGE,"E2"),sQuery(id+"F0.wireOp",EDGE,"E3"),sQuery(id+"F0.wireOp",EDGE,"E4"),sQuery(id+"F0.wireOp",EDGE,"E5"),sQuery(id+"F0.wireOp",EDGE,"E6"),sQuery(id+"F0.wireOp",EDGE,"E7"),sQuery(id+"F0.wireOp",EDGE,"E8"),sQuery(id+"F0.wireOp",EDGE,"E9"),sQuery(id+"F0.wireOp",EDGE,"E10"),sQuery(id+"F0.wireOp",EDGE,"E11"),sQuery(id+"F0.wireOp",EDGE,"E12"),sQuery(id+"F0.wireOp",EDGE,"E13"),sQuery(id+"F0.wireOp",EDGE,"E14.filletArc"),sQuery(id+"F0.wireOp",EDGE,"E15.filletArc"),sQuery(id+"F0.wireOp",EDGE,"E16.filletArc"),sQuery(id+"F0.wireOp",EDGE,"E17.trimOffspring"),sQuery(id+"F0.wireOp",EDGE,"E18"),sQuery(id+"F0.wireOp",EDGE,"E19"),sQuery(id+"F0.wireOp",EDGE,"E20"),sQuery(id+"F0.wireOp",EDGE,"E21.filletArc"),sQuery(id+"F0.wireOp",EDGE,"E22.filletArc"),sQuery(id+"F0.wireOp",EDGE,"E23.filletArc"),sQuery(id+"F0.wireOp",EDGE,"E24.trimOffspring"),sQuery(id+"F0.wireOp",EDGE,"E25"),sQuery(id+"F0.wireOp",EDGE,"E26"),sQuery(id+"F0.wireOp",EDGE,"E27"),sQuery(id+"F0.wireOp",EDGE,"E28.filletArc"),sQuery(id+"F0.wireOp",EDGE,"E29.filletArc"),sQuery(id+"F0.wireOp",EDGE,"E30.filletArc"),sQuery(id+"F0.wireOp",EDGE,"E31.trimOffspring"),sQuery(id+"F0.wireOp",EDGE,"E32.trimOffspring"),sQuery(id+"F0.wireOp",EDGE,"E33.trimOffspring"),sQuery(id+"F0.wireOp",EDGE,"E34.filletArc"),sQuery(id+"F0.wireOp",EDGE,"E35.filletArc"),sQuery(id+"F0.wireOp",EDGE,"E36.filletArc"),sQuery(id+"F0.wireOp",EDGE,"E37.filletArc"),sQuery(id+"F0.wireOp",EDGE,"E38.filletArc"),sQuery(id+"F0.wireOp",EDGE,"E39.filletArc")])]});
            var Q10;
            Q10=makeQuery(id+"F2.opExtrude","SWEPT_BODY",BODY,{"disambiguationData":[OSD([sQuery(id+"F0.wireOp",EDGE,"E0"),sQuery(id+"F0.wireOp",EDGE,"E1"),sQuery(id+"F0.wireOp",EDGE,"E2"),sQuery(id+"F0.wireOp",EDGE,"E3"),sQuery(id+"F0.wireOp",EDGE,"E4"),sQuery(id+"F0.wireOp",EDGE,"E5"),sQuery(id+"F0.wireOp",EDGE,"E6"),sQuery(id+"F0.wireOp",EDGE,"E7"),sQuery(id+"F0.wireOp",EDGE,"E8"),sQuery(id+"F0.wireOp",EDGE,"E9"),sQuery(id+"F0.wireOp",EDGE,"E10"),sQuery(id+"F0.wireOp",EDGE,"E11"),sQuery(id+"F0.wireOp",EDGE,"E12"),sQuery(id+"F0.wireOp",EDGE,"E13"),sQuery(id+"F0.wireOp",EDGE,"E14.filletArc"),sQuery(id+"F0.wireOp",EDGE,"E15.filletArc"),sQuery(id+"F0.wireOp",EDGE,"E16.filletArc"),sQuery(id+"F0.wireOp",EDGE,"E17.trimOffspring"),sQuery(id+"F0.wireOp",EDGE,"E18"),sQuery(id+"F0.wireOp",EDGE,"E19"),sQuery(id+"F0.wireOp",EDGE,"E20"),sQuery(id+"F0.wireOp",EDGE,"E21.filletArc"),sQuery(id+"F0.wireOp",EDGE,"E22.filletArc"),sQuery(id+"F0.wireOp",EDGE,"E23.filletArc"),sQuery(id+"F0.wireOp",EDGE,"E24.trimOffspring"),sQuery(id+"F0.wireOp",EDGE,"E25"),sQuery(id+"F0.wireOp",EDGE,"E26"),sQuery(id+"F0.wireOp",EDGE,"E27"),sQuery(id+"F0.wireOp",EDGE,"E28.filletArc"),sQuery(id+"F0.wireOp",EDGE,"E29.filletArc"),sQuery(id+"F0.wireOp",EDGE,"E30.filletArc"),sQuery(id+"F0.wireOp",EDGE,"E31.trimOffspring"),sQuery(id+"F0.wireOp",EDGE,"E32.trimOffspring"),sQuery(id+"F0.wireOp",EDGE,"E33.trimOffspring"),sQuery(id+"F0.wireOp",EDGE,"E34.filletArc"),sQuery(id+"F0.wireOp",EDGE,"E35.filletArc"),sQuery(id+"F0.wireOp",EDGE,"E36.filletArc"),sQuery(id+"F0.wireOp",EDGE,"E37.filletArc"),sQuery(id+"F0.wireOp",EDGE,"E38.filletArc"),sQuery(id+"F0.wireOp",EDGE,"E39.filletArc")])]});
            booleanBodies(context, id + "F21", {"operationType" : BooleanOperationType.SUBTRACTION, "tools" : qUnion([Q0, Q1, Q2, Q3, Q4, Q5, Q6, Q7, Q8]), "targets" : qUnion([Q9, Q10])});
        }
        {
            var Q0;
            Q0=makeQuery(id+"F1.opExtrude","CAP_FACE",FACE,{"disambiguationData":[OSD([sQuery(id+"F0.wireOp",EDGE,"E0"),sQuery(id+"F0.wireOp",EDGE,"E1"),sQuery(id+"F0.wireOp",EDGE,"E2"),sQuery(id+"F0.wireOp",EDGE,"E3"),sQuery(id+"F0.wireOp",EDGE,"E4"),sQuery(id+"F0.wireOp",EDGE,"E5"),sQuery(id+"F0.wireOp",EDGE,"E6"),sQuery(id+"F0.wireOp",EDGE,"E7"),sQuery(id+"F0.wireOp",EDGE,"E8"),sQuery(id+"F0.wireOp",EDGE,"E9"),sQuery(id+"F0.wireOp",EDGE,"E10"),sQuery(id+"F0.wireOp",EDGE,"E11"),sQuery(id+"F0.wireOp",EDGE,"E12"),sQuery(id+"F0.wireOp",EDGE,"E13"),sQuery(id+"F0.wireOp",EDGE,"E14.filletArc"),sQuery(id+"F0.wireOp",EDGE,"E15.filletArc"),sQuery(id+"F0.wireOp",EDGE,"E16.filletArc"),sQuery(id+"F0.wireOp",EDGE,"E17.trimOffspring"),sQuery(id+"F0.wireOp",EDGE,"E18"),sQuery(id+"F0.wireOp",EDGE,"E19"),sQuery(id+"F0.wireOp",EDGE,"E20"),sQuery(id+"F0.wireOp",EDGE,"E21.filletArc"),sQuery(id+"F0.wireOp",EDGE,"E22.filletArc"),sQuery(id+"F0.wireOp",EDGE,"E23.filletArc"),sQuery(id+"F0.wireOp",EDGE,"E24.trimOffspring"),sQuery(id+"F0.wireOp",EDGE,"E25"),sQuery(id+"F0.wireOp",EDGE,"E26"),sQuery(id+"F0.wireOp",EDGE,"E27"),sQuery(id+"F0.wireOp",EDGE,"E28.filletArc"),sQuery(id+"F0.wireOp",EDGE,"E29.filletArc"),sQuery(id+"F0.wireOp",EDGE,"E30.filletArc"),sQuery(id+"F0.wireOp",EDGE,"E31.trimOffspring"),sQuery(id+"F0.wireOp",EDGE,"E32.trimOffspring"),sQuery(id+"F0.wireOp",EDGE,"E33.trimOffspring"),sQuery(id+"F0.wireOp",EDGE,"E34.filletArc"),sQuery(id+"F0.wireOp",EDGE,"E35.filletArc"),sQuery(id+"F0.wireOp",EDGE,"E36.filletArc"),sQuery(id+"F0.wireOp",EDGE,"E37.filletArc"),sQuery(id+"F0.wireOp",EDGE,"E38.filletArc"),sQuery(id+"F0.wireOp",EDGE,"E39.filletArc")])],"isStart":false});
            var Q1;
            Q1=makeQuery(id+"F2.opExtrude","CAP_FACE",FACE,{"disambiguationData":[OSD([sQuery(id+"F0.wireOp",EDGE,"E0"),sQuery(id+"F0.wireOp",EDGE,"E1"),sQuery(id+"F0.wireOp",EDGE,"E2"),sQuery(id+"F0.wireOp",EDGE,"E3"),sQuery(id+"F0.wireOp",EDGE,"E4"),sQuery(id+"F0.wireOp",EDGE,"E5"),sQuery(id+"F0.wireOp",EDGE,"E6"),sQuery(id+"F0.wireOp",EDGE,"E7"),sQuery(id+"F0.wireOp",EDGE,"E8"),sQuery(id+"F0.wireOp",EDGE,"E9"),sQuery(id+"F0.wireOp",EDGE,"E10"),sQuery(id+"F0.wireOp",EDGE,"E11"),sQuery(id+"F0.wireOp",EDGE,"E12"),sQuery(id+"F0.wireOp",EDGE,"E13"),sQuery(id+"F0.wireOp",EDGE,"E14.filletArc"),sQuery(id+"F0.wireOp",EDGE,"E15.filletArc"),sQuery(id+"F0.wireOp",EDGE,"E16.filletArc"),sQuery(id+"F0.wireOp",EDGE,"E17.trimOffspring"),sQuery(id+"F0.wireOp",EDGE,"E18"),sQuery(id+"F0.wireOp",EDGE,"E19"),sQuery(id+"F0.wireOp",EDGE,"E20"),sQuery(id+"F0.wireOp",EDGE,"E21.filletArc"),sQuery(id+"F0.wireOp",EDGE,"E22.filletArc"),sQuery(id+"F0.wireOp",EDGE,"E23.filletArc"),sQuery(id+"F0.wireOp",EDGE,"E24.trimOffspring"),sQuery(id+"F0.wireOp",EDGE,"E25"),sQuery(id+"F0.wireOp",EDGE,"E26"),sQuery(id+"F0.wireOp",EDGE,"E27"),sQuery(id+"F0.wireOp",EDGE,"E28.filletArc"),sQuery(id+"F0.wireOp",EDGE,"E29.filletArc"),sQuery(id+"F0.wireOp",EDGE,"E30.filletArc"),sQuery(id+"F0.wireOp",EDGE,"E31.trimOffspring"),sQuery(id+"F0.wireOp",EDGE,"E32.trimOffspring"),sQuery(id+"F0.wireOp",EDGE,"E33.trimOffspring"),sQuery(id+"F0.wireOp",EDGE,"E34.filletArc"),sQuery(id+"F0.wireOp",EDGE,"E35.filletArc"),sQuery(id+"F0.wireOp",EDGE,"E36.filletArc"),sQuery(id+"F0.wireOp",EDGE,"E37.filletArc"),sQuery(id+"F0.wireOp",EDGE,"E38.filletArc"),sQuery(id+"F0.wireOp",EDGE,"E39.filletArc")])],"isStart":false});
            fillet(context, id + "F22", {"entities" : qUnion([Q0, Q1]), "radius" : .2 * mm, "tangentPropagation" : true, "allowEdgeOverflow" : false});
        }
    });
